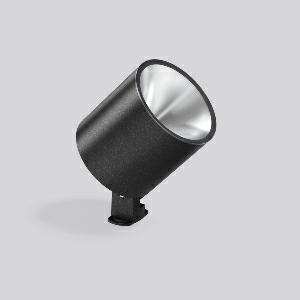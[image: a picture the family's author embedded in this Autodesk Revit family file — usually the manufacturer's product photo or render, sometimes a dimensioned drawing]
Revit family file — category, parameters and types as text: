
# Revit family: andho_midi_mast_722272_0031_2_76_0ded
name_source: partatom
category: Lighting Fixtures
units: mm (PartAtom-declared; Revit-internal decimal feet)

## family parameters
Cut with Voids When Loaded = No
Host = Face
Light Source = No
Part Type = Normal
Room Calculation Point = No
Round Connector Dimension = Use Diameter
Shared = No

## types (1)
- ANDHO midi Mast (1 x LED Modul 827, 4700 lm, 2700)
    Apparent Load = 39 VA
    Approval mark = CE
    CIE Flux Codes = 95 98 99 100 100
    Color Rendering = 80
    Color Temperature = 2700
    Default Elevation = 1800 mm
    Description = Series: ANDHO midi
Surface-mounted LED projector in a timeless design. Housing: die-cast aluminium, seawater resistant powder-coated. Integral membrane valve for pressure compensation and avoidance of condensation. MIRO-SILVER reflectors for outstanding efficiency or polycarbonate lenses for the best uniformity of the light cone. Cover clear single-pane toughened glass, edge printed. COB LED with socket for easy replacement. Projector: horizontal rotation range: 40°, vertical swivel range: 90°. Lockable projector orientation. Driver integrated. 
Colour: anthracite metallic (DB703)
Length: 261 mm
Width: 154 mm
Height: 216 mm
Lamp: LED
System power: 39 W
Rated luminous flux: 4700 lm
Luminous efficiency: 121 lm/W
Control gear: Converter, dimmable, DALI
Protection class: II
Type of protection: IP 65
    Height = 216 mm
    Lamp = 1 x LED Modul 827
    Lamp Light Flux = 4700 lm
    Lamp count = 1
    Length = 261 mm
    Lifetime = 50000 h
    Luminous efficacy = 121 lm/W
    Manufacturer = RZB
    ModVariant = No
    Model = 722272.0031.2.76
    Mounting Place = Ceiling, Wall
    Mounting Type = Surface mounted
    Number of Poles = 1
    OnlyDefault = Yes
    Power Factor = 1
    Product Name = ANDHO midi Mast
    Product group = Floodlights and spotlights
    ProductGroupID = 1354
    Protection Class = Protection class II
    Protection Degree = IP 65
    RLX_Detail_Level = 1
    RLX_Emergency_Light_Flux = 0 lm
    RLX_Emergency_Type = 0
    RLX_Emergency_Type_DB = No
    RlxData = <blob elided: 55041 chars, md5=aa0eb280>
    Socket = socket
    Standby Power = 0 W
    System Light Flux = 4700 lm
    System Power = 39 W
    Type Comments = Product without accessories
    Type Image = 722270.0031.76.jpg
    URL = http://relux.com
    VarID = ---
    Voltage = 230 V
    Voltage Range = 220-240 V
    Weight = 0.00 kg
    Width = 154 mm

## geometry (parser evidence)
native form markers: Blend x4, Sweep x15
no freeform markers — native parametric forms only
